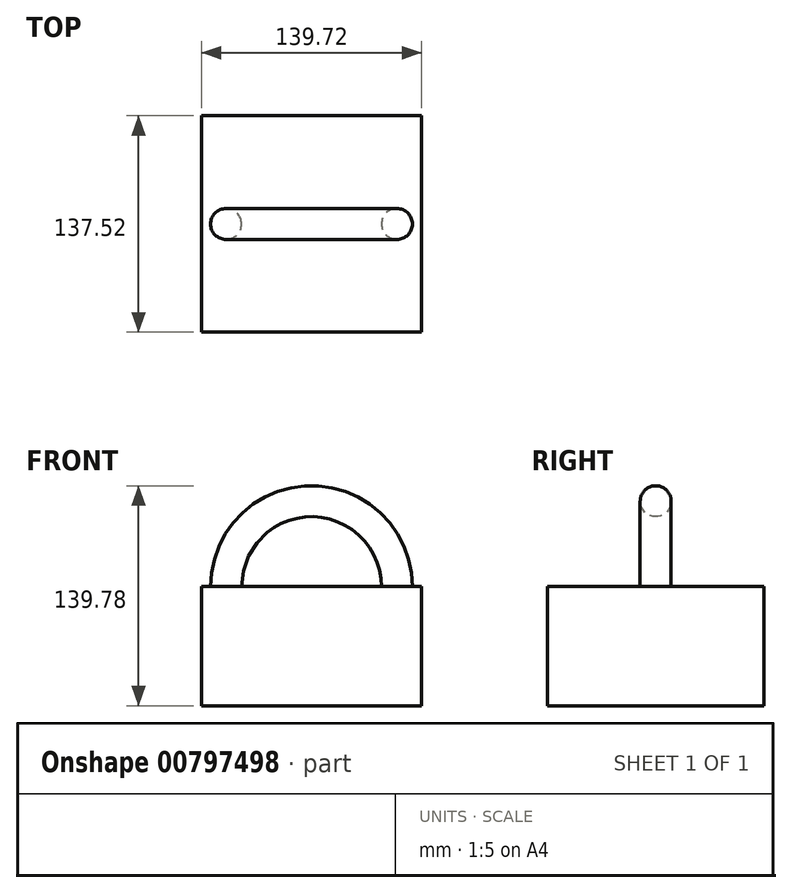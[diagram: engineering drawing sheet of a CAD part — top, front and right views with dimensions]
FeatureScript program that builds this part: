
annotation { "Feature Type Name" : "Feature", "Feature Type Description" : "" }
export const myFeature = defineFeature(function(context is Context, id is Id, definition is map)
    precondition{}
    {
        {
            var Q0;
            Q0=qCreatedBy(makeId("Top.planeOp"),FACE);
            var sketch = newSketch(context, id + "F0", { "sketchPlane" : qUnion([Q0])});
            skLineSegment(sketch, "E0.bottom", {"start": v(69.86, -68.76) * mm, "end": v(-69.86, -68.76) * mm});
            skLineSegment(sketch, "E0.top", {"start": v(69.86, 68.76) * mm, "end": v(-69.86, 68.76) * mm});
            skLineSegment(sketch, "E0.left", {"start": v(69.86, -68.76) * mm, "end": v(69.86, 68.76) * mm});
            skLineSegment(sketch, "E0.right", {"start": v(-69.86, -68.76) * mm, "end": v(-69.86, 68.76) * mm});
            skPoint(sketch, "E0.middle", {"position": v(0, 0) * mm});
            skLineSegment(sketch, "E1", {"start": v(0, 68.76) * mm, "end": v(0, -68.76) * mm});
            skSolve(sketch);
        }
        {
            var Q0;
            Q0=qCreatedBy(makeId("Top.planeOp"),FACE);
            var sketch = newSketch(context, id + "F1", { "sketchPlane" : qUnion([Q0])});
            skCircle(sketch, "E2", {"center": v(54.26, 0) * mm, "radius": 9.82 * mm});
            skSolve(sketch);
        }
        {
            var Q0;
            {var subQ0=sQuery(id+"F0.wireOp",EDGE,"E0.left");Q0=makeQuery(id+"F0.imprint","IMPRINT",FACE,{"disambiguationData":[TD([[makeQuery(id+"F0.imprint","IMPRINT",EDGE,{"derivedFrom":subQ0}),1.0]])]});}
            var Q1;
            {var subQ0=sQuery(id+"F0.wireOp",EDGE,"E0.right");Q1=makeQuery(id+"F0.imprint","IMPRINT",FACE,{"disambiguationData":[TD([[makeQuery(id+"F0.imprint","IMPRINT",EDGE,{"derivedFrom":subQ0}),-1.0]])]});}
            extrude(context, id + "F2", {"entities" : qUnion([Q0, Q1]), "oppositeDirection" : true, "depth" : 75.7 * mm, "offsetDistance" : 25.4 * mm});
        }
        {
            var Q0;
            Q0 = qSketchRegion(id + "F1", true);
            var Q1;
            Q1=sQuery(id+"F0.wireOp",EDGE,"E1");
            revolve(context, id + "F3", {"operationType" : NewBodyOperationType.ADD, "surfaceOperationType" : NewSurfaceOperationType.NEW, "entities" : qUnion([Q0]), "axis" : qUnion([Q1]), "revolveType" : RevolveType.FULL});
        }
    });
